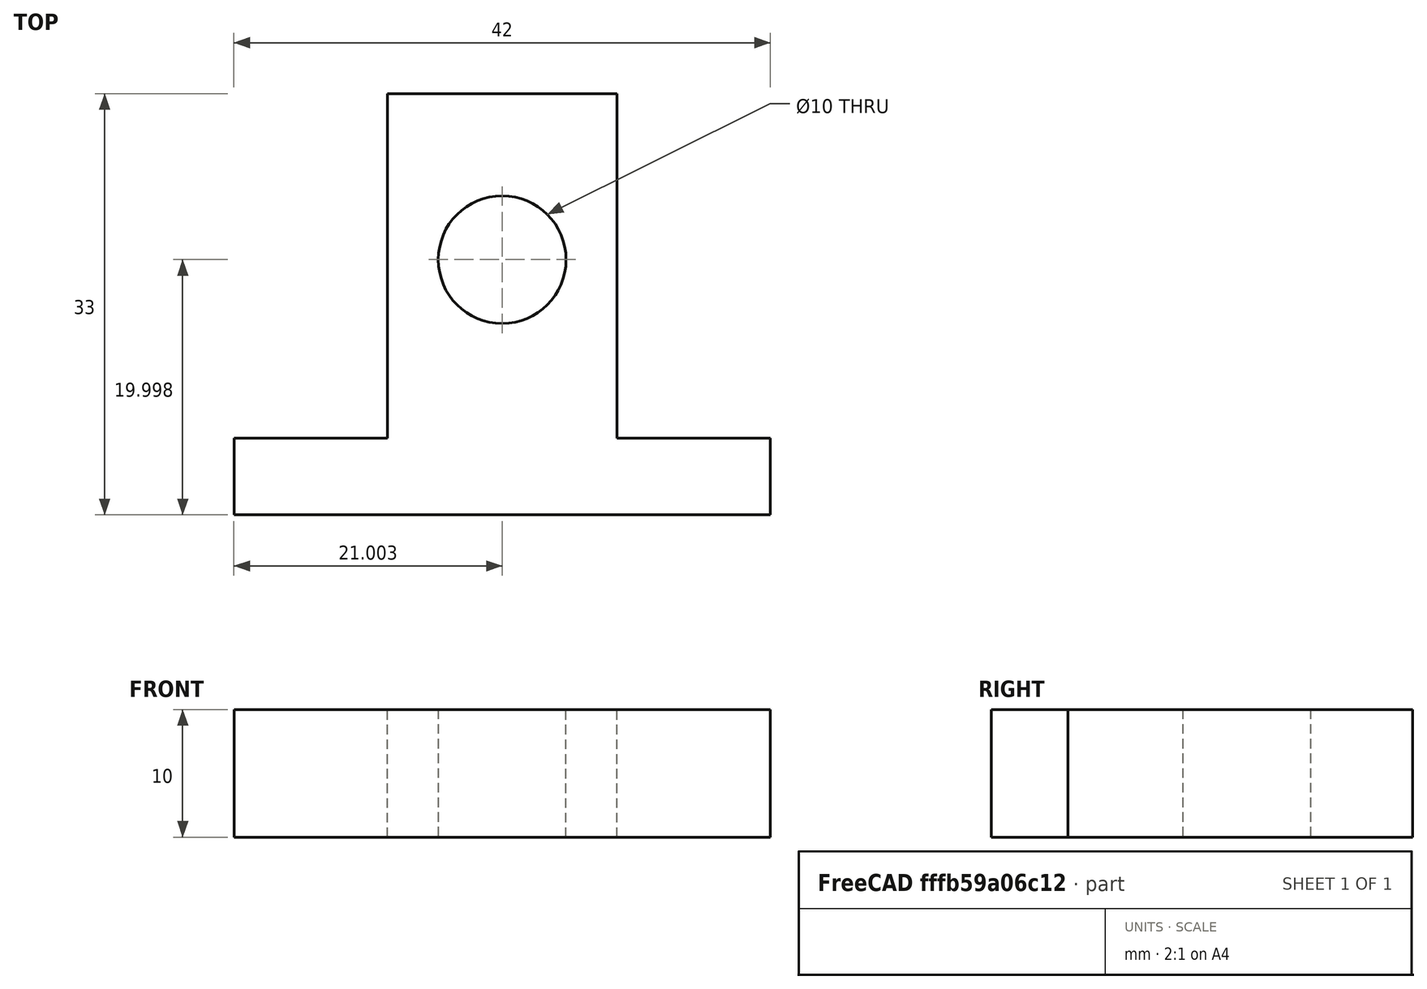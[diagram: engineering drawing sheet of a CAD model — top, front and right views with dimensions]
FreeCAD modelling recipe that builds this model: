
FCSTD DOCUMENT  (FreeCAD 0.17R13522 (Git))
Label: SuporteDeEixoSK10
License: All rights reserved
LicenseURL: http://en.wikipedia.org/wiki/All_rights_reserved
objects: Sketcher::SketchObject×1, Part::Extrusion×1
note: 2 computed .brp shape members not serialized (recipe doc carries the construction recipe); baked Part::Feature solids carry a one-line shape summary decoded from their .brp

FEATURE [Sketcher::SketchObject] Sketch
  sketch-geometry (9):
    g0: LineSegment StartX=28.5226 StartY=37.1384 StartZ=0 EndX=28.5226 EndY=43.1384 EndZ=0
    g1: LineSegment StartX=28.5226 StartY=43.1384 StartZ=0 EndX=40.5226 EndY=43.1384 EndZ=0
    g2: LineSegment StartX=40.5226 StartY=43.1384 StartZ=0 EndX=40.5226 EndY=70.1384 EndZ=0
    g3: LineSegment StartX=40.5226 StartY=70.1384 StartZ=0 EndX=58.5226 EndY=70.1384 EndZ=0
    g4: LineSegment StartX=58.5226 StartY=70.1384 StartZ=0 EndX=58.5226 EndY=43.1384 EndZ=0
    g5: LineSegment StartX=58.5226 StartY=43.1384 StartZ=0 EndX=70.5226 EndY=43.1384 EndZ=0
    g6: LineSegment StartX=70.5226 StartY=43.1384 StartZ=0 EndX=70.5226 EndY=37.1384 EndZ=0
    g7: LineSegment StartX=70.5226 StartY=37.1384 StartZ=0 EndX=28.5226 EndY=37.1384 EndZ=0
    g8: Circle CenterX=49.5226 CenterY=57.1384 CenterZ=0 NormalX=0 NormalY=0 NormalZ=1 AngleXU=0 Radius=5
  constraints (26):
    c: Vertical(g0)
    c: Coincident(g0,g1)
    c: Coincident(g1,g2)
    c: Vertical(g2)
    c: Coincident(g2,g3)
    c: Horizontal(g3)
    c: Coincident(g3,g4)
    c: Vertical(g4)
    c: Coincident(g4,g5)
    c: Coincident(g5,g6)
    c: Vertical(g6)
    c: Coincident(g6,g7)
    c: Coincident(g7,g0)
    c: Horizontal(g7)
    c: Horizontal(g1)
    c: Horizontal(g5)
    c: Equal(g0,g6)
    c: Equal(g2,g4)
    c: Equal(g1,g5)
    c: DistanceY(g0,g0) = 6
    c: DistanceY(g2,g2) = 27
    c: DistanceX(g3,g3) = 18
    c: DistanceX(g7,g7) = 42
    c: Radius(g8) = 5
    c: DistanceY(g8,g3) = 13
    c: DistanceX(g2,g8) = 9
FEATURE [Part::Extrusion] Extrude  label="SK10"
  Base = -> Sketch
  Dir = (0,0,14)
  DirMode = 0
  FaceMakerClass = Part::FaceMakerBullseye
  LengthFwd = 10
  LengthRev = 0
  Placement = pos=(59,0,0) rot=(0,0,1;0rad)
  Solid = true
  Symmetric = false
